# Revit family: PRD_AR_ShwrFttngsPckg_ShowerPanel_F5ET2020-21_2024-26
name_source: partatom
category: Plumbing Fixtures
revit_build: Autodesk Revit 2018 (Build: 20190510_1515(x64)
units: mm (PartAtom-declared; Revit-internal decimal feet)

## family parameters
Cut with Voids When Loaded = No
Host = Face
OmniClass Number = 23.45.05.14.17
OmniClass Title = Showers
Part Type = Normal
Room Calculation Point = No
Round Connector Dimension = Use Diameter
Shared = No

## types (5) — shared parameters
AdditionalConnections = No
AdjustableFlowTime = Yes
AssetType = Fixed
CasingMaterial = PRD_AR_StainlessSteel_SatinFinished_Dark
Category = Pr_40_20_87_75, Shower fittings package
Circulation = No
ConnectionWithPayWaterDispenser = via electronic module
Default Elevation = 1500 mm  [stored 4.92126 ft]
DefaultAutomaticHygieneFlushing = 24h after the last activity
DurationUnit = year
FittingMaterial = PRD_AR_ChromatedBrass_HighPolished
FlowColdWater = 0.2 L/s
FlowHotWater = 0.2 L/s
FunctionalPrinciple = Electronic self-closing
HygieneFlushing = Yes
IfcExportAs = IfcSanitaryTerminalType
IfcExportType = SHOWER
InletSize = G-1-2-A
Manufacturer = KWC Group AG
ManufacturerName = KWC Group AG
ManufacturerURL = www.kwc.com
MaximumFlowTime = 255.00 seconds
MinimumFlowTime = 1.00 seconds
NBSDescription = Shower fittings package
NBSReference = 45-35-70/330
NominalHeight = 1160 mm  [stored 3.80577 ft]
NominalWidth = 235 mm  [stored 0.770997 ft]
PositionOfPowerConnection = Top backside
PositionOfWaterConnection = From top / backside
PowerConsumption = 1.5
PowerSupplyConnection = 6,75 / 12 V DC / A3000 open
ProductInformation = https://pim.kwc.com
ProtectiveShutdown = Yes
ProtectiveSystemIP = IP 59K
ShowerPipeDraining = No
ShowerType = Individual
SoundInsulation = No
TailorMade = No
ThermalDisinfection = Prepared for automatic thermal disinfection
TubeMaterial = PRD_AR_StainlessSteel_SatinFinished
TypeOfMixing = Thermostat
TypeOfMounting = Wall mounting
TypeOfOperation = Sensor operation
TypeOfSensor = Opto-electronic sensor
TypeOfShower = Shower panel
URL = www.kwc.com
Uniclass2015Code = Pr_40_20_87_75
Uniclass2015Title = Shower fittings package
Uniclass2015Version = Products v1.17
Version = 1
WarrantyDurationUnit = year
zero-valued in all types: DrainSize

## per-type parameters (varying)
| type | BIMObjectName | BodyMaterial | Color | ColorCasing | Description | Features | Finish | GrossWeight | HandShowerFittingOffset | HandShowerVisibility | HasTray | IntegralAccessories | Material | MaterialCode | MinimumFlowPressure | ModelNumber | Name | NetWeight | NominalDepth | ShelfVisibility | Size | VolumeFlowRate |
| F5ET2020 | PRD_AR_ShowerFittingsPackage_ShowerPanel_F5ET2020 | PRD_AR_StainlessSteel_SatinFinished | stainless steel | Yes | F5E Therm shower panel made of stainless steel for wall mounting with thermostatic mixer and connecting nozzles for the shower head. Electrically controlled, for connection to hot water and cold water. Shower valve with integrated solenoid valve cartridge, thermostat and mechanism for optional bypass solenoid valve cartridge to perform program-controlled thermal disinfection. Thermostat with metal handle, an adjustable and turn-proof temperature stop and an option for manual thermal disinfection. All-metal construction, visible parts high-polished or chrome-plated. Connecting nozzles for the required additional DN 15 KWC shower head with pre-fitted flow regulator 9.0 l/min. Housing made of stainless steel with raised function surface and plastic cover caps. Button sensor including control electronics with start/stop function and deactivation for cleaning. Connecting hoses with lockable water volume control with backflow preventer and strainer. Activated water hygiene flushing 24 hours after last activation and saving of statistical data. With option for parameterization and communication via the optional bidirectional remote control. Battery operation with 6 V lithium battery (CR-P2) per fitting, separate power supply via plug-in power supply unit 6.75 V/12 V DC or AQUA 3000 open system accessories. | stainless steel, with thermostatic mixer, electrically controlled | satin finished | 9.40 kg | 0 mm  [stored 0 ft] | No | No | shower head and battery compartment including battery or plug-in power supply unit with extension cable to be ordered separately | stainless steel | 1.4301 | 1.50 bar | 2030054250 | Shower Panel F5ET2020 | 9.10 kg | 90 mm  [stored 0.295276 ft] | No | 235 x 1160 x 90 mm (W x H x D) | 0.15 L/s at 3 bar |
| F5ET2021 | PRD_AR_ShowerFittingsPackage_ShowerPanel_F5ET2021 | PRD_AR_StainlessSteel_SatinFinished | stainless steel | Yes | F5E Therm shower panel made of stainless steel for wall mounting with thermostatic mixer and a hand shower fitting. Electrically controlled, for connection to hot water and cold water. Shower valve with integrated solenoid valve cartridge, thermostat and mechanism for optional bypass solenoid valve cartridge to perform program-controlled thermal disinfection. Thermostat with metal handle, an adjustable and turn-proof temperature stop and an option for manual thermal disinfection. All-metal construction, visible parts high-polished or chrome-plated. Pre-fitted chrome-plated brass shower pole with height-adjustable hand shower holder and chrome-plated plastic hand shower, shower head with rain jet, diameter 110 mm, shower hose 900 mm. Housing made of stainless steel with raised function surface and plastic cover caps. Button sensor including control electronics with start/stop function and deactivation for cleaning. Connecting hoses with lockable water volume control with backflow preventer and strainer. Activated water hygiene flushing 24 hours after last activation and saving of statistical data. With option for parameterization and communication via the optional bidirectional remote control. Battery operation with 6 V lithium battery (CR-P2) per fitting, separate power supply via plug-in power supply unit 6.75 V / 12 V DC or AQUA 3000 open system accessories. | stainless steel, with thermostatic mixer and a hand shower fitting, electrically controlled | satin finished | 10.40 kg | 0 mm  [stored 0 ft] | Yes | No | battery compartment including battery or plug-in power supply unit with extension cable to be ordered separately | stainless steel | 1.4301 | 1.00 bar | 2030056562 | Shower Panel F5ET2021 | 9.88 kg | 90 mm  [stored 0.295276 ft] | No | 235 x 1160 x 90 mm (W x H x D) |  |
| F5ET2024 | PRD_AR_ShowerFittingsPackage_ShowerPanel_F5ET2024 | PRD_AR_MineralMaterial_Chromed | alpine white | No | F5E Therm shower panel made of mineral material for wall mounting with thermostatic mixer and connecting nozzles for the shower head. Electrically controlled, for connection to hot water and cold water. Shower valve with integrated solenoid valve cartridge, thermostat and mechanism for optional bypass solenoid valve cartridge to perform program-controlled thermal disinfection. Thermostat with metal handle, an adjustable and turn-proof temperature stop and an option for manual thermal disinfection. All-metal construction, visible parts high-polished or chrome-plated. Connecting nozzles for the required additional DN 15 KWC shower head with pre-fitted flow regulator 9.0 l/min. Housing with raised function surface made of MIRANIT resin-bonded mineral material with pore-free smooth surface (temperature-resistant up to 80°C), Alpine white colour. Button sensor including control electronics with start/stop function and deactivation for cleaning. Connecting hoses with lockable water volume control with backflow preventer and strainer. Activated water hygiene flushing 24 hours after last activation and saving of statistical data. With option for parameterization and communication via the optional bidirectional remote control. Battery operation with 6 V lithium battery (CR-P2) per fitting, separate power supply via plug-in power supply unit 6.75 V/12 V DC or AQUA 3000 open system accessories. | mineral material, with thermostatic mixer, electrically controlled | chromed | 12.10 kg | 10 mm  [stored 0.0328084 ft] | No | No | shower head and battery compartment including battery or plug-in power supply unit with extension cable to be ordered separately | mineral material | Miranit | 1.50 bar | 2030056563 | Shower Panel F5ET2024 | 11.50 kg | 100 mm  [stored 0.328084 ft] | No | 235 x 1160 x 100 mm (W x H x D) | 0.15 L/s at 3 bar |
| F5ET2025 | PRD_AR_ShowerFittingsPackage_ShowerPanel_F5ET2025 | PRD_AR_MineralMaterial_Chromed | alpine white | No | F5E Therm shower panel made of mineral material for wall mounting with thermostatic mixer and a hand shower fitting. Electrically controlled, for connection to hot water and cold water. Shower valve with integrated solenoid valve cartridge, thermostat and mechanism for optional bypass solenoid valve cartridge to perform program-controlled thermal disinfection. Thermostat with metal handle, an adjustable and turn-proof temperature stop and an option for manual thermal disinfection. All-metal construction, visible parts high-polished or chrome-plated. Pre-fitted chrome-plated brass shower pole with height-adjustable hand shower holder and chrome-plated plastic hand shower, shower head with rain jet, diameter 110 mm, shower hose 900 mm. Housing with raised function surface made of MIRANIT resin-bonded mineral material with pore-free smooth surface (temperature-resistant up to 80°C), Alpine white colour. Button sensor including control electronics with start/stop function and deactivation for cleaning. Connecting hoses with lockable water volume control with backflow preventer and strainer. Activated water hygiene flushing 24 hours after last activation and saving of statistical data. With option for parameterization and communication via the optional bidirectional remote control. Battery operation with 6 V lithium battery (CR-P2) per fitting, separate power supply via plug-in power supply unit 6.75 V/12 V DC or AQUA 3000 open system accessories. | mineral material, with thermostatic mixer and a hand shower fitting, electrically controlled | chromed | 16.50 kg | 10 mm  [stored 0.0328084 ft] | Yes | No | battery compartment including battery or plug-in power supply unit with extension cable to be ordered separately | mineral material | Miranit | 1.00 bar | 2030056573 | Shower Panel F5ET2025 | 15.00 kg | 100 mm  [stored 0.328084 ft] | No | 235 x 1160 x 100 mm (W x H x D) |  |
| F5ET2026 | PRD_AR_ShowerFittingsPackage_ShowerPanel_F5ET2026 | PRD_AR_MineralMaterial_Chromed | alpine white | No | F5E Therm shower panel made of mineral material for wall mounting with thermostatic mixer and connecting nozzles for the shower head. Electrically controlled, for connection to hot water and cold water. Shower valve with integrated solenoid valve cartridge, thermostat and mechanism for optional bypass solenoid valve cartridge to perform program-controlled thermal disinfection. Thermostat with metal handle, an adjustable and turn-proof temperature stop and an option for manual thermal disinfection. All-metal construction, visible parts high-polished or chrome-plated. Connecting nozzles for the required additional DN 15 KWC shower head with pre-fitted flow regulator 9.0 l/min. Housing with raised function surface and seamless moulded shower gel shelf made of MIRANIT resin-bonded mineral material with pore-free smooth surface (temperature-resistant up to 80°C), Alpine white colour. Button sensor including control electronics with start/stop function and deactivation for cleaning. Connecting hoses with lockable water volume control with backflow preventer and strainer. Activated water hygiene flushing 24 hours after last activation and saving of statistical data. With option for parameterization and communication via the optional bidirectional remote control. Battery operation with 6 V lithium battery (CR-P2) per fitting, separate power supply via plug-in power supply unit 6.75 V/12 V DC or AQUA 3000 open system accessories. | mineral material, with thermostatic mixer, electrically controlled | chromed | 13.15 kg | 10 mm  [stored 0.0328084 ft] | No | Yes | shower head and battery compartment including battery or plug-in power supply unit with extension cable to be ordered separately | mineral material | Miranit | 1.50 bar | 2030056574 | Shower Panel F5ET2026 | 12.40 kg | 100 mm  [stored 0.328084 ft] | Yes | 235 x 1160 x 100 mm (W x H x D) | 0.15 L/s at 3 bar |

note: column(s) folded — value = type name in every type: Model, ModelReference

note: [stored X ft] marks values corroborated as IEEE doubles in the binary element streams (Revit-internal decimal feet)

## geometry (parser evidence)
native form markers: Extrusion x2, Sweep x6
no freeform markers — native parametric forms only
